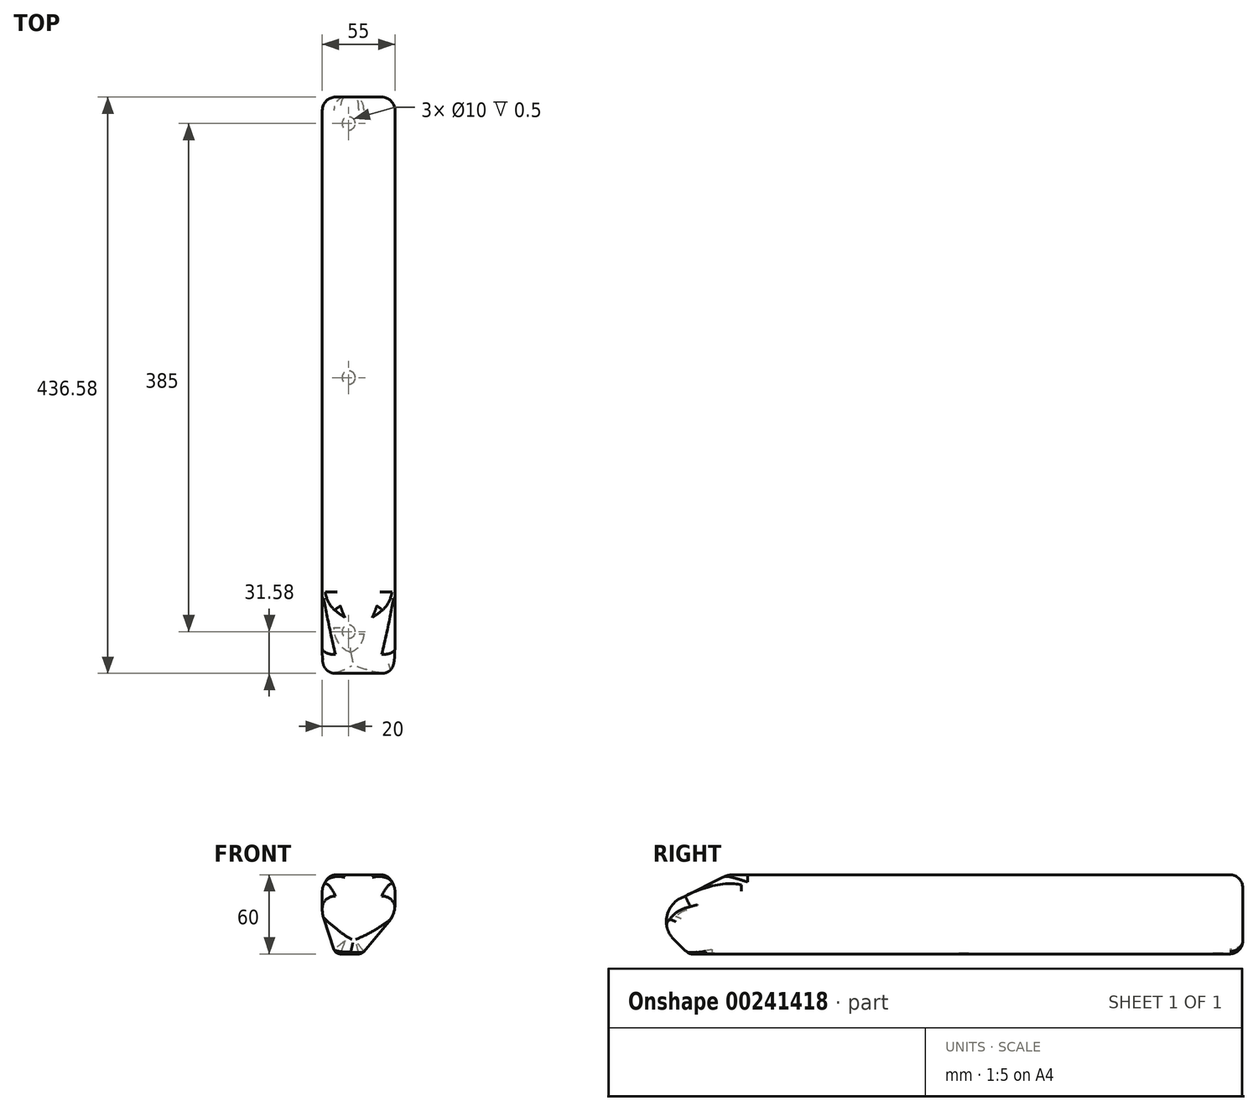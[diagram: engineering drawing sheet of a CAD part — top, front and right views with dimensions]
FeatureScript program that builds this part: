
annotation { "Feature Type Name" : "Feature", "Feature Type Description" : "" }
export const myFeature = defineFeature(function(context is Context, id is Id, definition is map)
    precondition{}
    {
        {
            var Q0;
            Q0=qCreatedBy(makeId("Top.planeOp"),FACE);
            var sketch = newSketch(context, id + "F0", { "sketchPlane" : qUnion([Q0])});
            skLineSegment(sketch, "E0.bottom", {"start": v(-27.5, 212.5) * mm, "end": v(27.5, 212.5) * mm});
            skLineSegment(sketch, "E0.top", {"start": v(-27.5, -237.5) * mm, "end": v(27.5, -237.5) * mm});
            skLineSegment(sketch, "E0.left", {"start": v(-27.5, 212.5) * mm, "end": v(-27.5, -237.5) * mm});
            skLineSegment(sketch, "E0.right", {"start": v(27.5, 212.5) * mm, "end": v(27.5, -237.5) * mm});
            skPoint(sketch, "E0.middle", {"position": v(0, -12.5) * mm});
            skSolve(sketch);
        }
        {
            var Q0;
            Q0 = qSketchRegion(id + "F0", true);
            extrude(context, id + "F1", {"entities" : qUnion([Q0]), "depth" : 60 * mm});
        }
        {
            var Q0;
            Q0=makeQuery(id+"F1.opExtrude","CAP_FACE",FACE,{"disambiguationData":[OSD([sQuery(id+"F0.wireOp",EDGE,"E0.bottom"),sQuery(id+"F0.wireOp",EDGE,"E0.top"),sQuery(id+"F0.wireOp",EDGE,"E0.left"),sQuery(id+"F0.wireOp",EDGE,"E0.right")])],"isStart":true});
            var sketch = newSketch(context, id + "F2", { "sketchPlane" : qUnion([Q0])});
            skCircle(sketch, "E1", {"center": v(-7.5, 192.5) * mm, "radius": 5 * mm});
            skCircle(sketch, "E2", {"center": v(-7.5, -192.5) * mm, "radius": 5 * mm});
            skCircle(sketch, "E3", {"center": v(-7.5, 0) * mm, "radius": 5 * mm});
            skSolve(sketch);
        }
        {
            var Q0;
            Q0 = qSketchRegion(id + "F2", true);
            extrude(context, id + "F3", {"entities" : qUnion([Q0]), "operationType" : NewBodyOperationType.REMOVE, "oppositeDirection" : true, "depth" : .5 * mm});
        }
        {
            var Q0;
            Q0=makeQuery(id+"F1.opExtrude","CAP_EDGE",EDGE,{"disambiguationData":[OSD([sQuery(id+"F0.wireOp",EDGE,"E0.top")])],"isStart":false});
            chamfer(context, id + "F4", {"entities" : qUnion([Q0]), "chamferType" : ChamferType.TWO_OFFSETS, "width1" : 60 * mm, "oppositeDirection" : false, "width2" : 30 * mm});
        }
        {
            var Q0;
            Q0=makeQuery(id+"F1.opExtrude","CAP_EDGE",EDGE,{"disambiguationData":[OSD([sQuery(id+"F0.wireOp",EDGE,"E0.top")])],"isStart":true});
            chamfer(context, id + "F5", {"entities" : qUnion([Q0]), "chamferType" : ChamferType.TWO_OFFSETS, "width1" : 30 * mm, "oppositeDirection" : false, "width2" : 30 * mm, "tangentPropagation" : true});
        }
        {
            var Q0;
            Q0=makeQuery(id+"F1.opExtrude","CAP_EDGE",EDGE,{"disambiguationData":[OSD([sQuery(id+"F0.wireOp",EDGE,"E0.left")])],"isStart":true});
            chamfer(context, id + "F6", {"entities" : qUnion([Q0]), "chamferType" : ChamferType.TWO_OFFSETS, "width1" : 30 * mm, "oppositeDirection" : false, "width2" : 10 * mm, "tangentPropagation" : true});
        }
        {
            var Q0;
            Q0=makeQuery(id+"F1.opExtrude","CAP_EDGE",EDGE,{"disambiguationData":[OSD([sQuery(id+"F0.wireOp",EDGE,"E0.right")])],"isStart":true});
            chamfer(context, id + "F7", {"entities" : qUnion([Q0]), "chamferType" : ChamferType.TWO_OFFSETS, "width1" : 25 * mm, "oppositeDirection" : false, "width2" : 30 * mm, "tangentPropagation" : true});
        }
        {
            var Q0;
            Q0=makeQuery(id+"F1.opExtrude","CAP_EDGE",EDGE,{"disambiguationData":[OSD([sQuery(id+"F0.wireOp",EDGE,"E0.left")])],"isStart":false});
            var Q1;
            Q1=makeQuery(id+"F1.opExtrude","CAP_EDGE",EDGE,{"disambiguationData":[OSD([sQuery(id+"F0.wireOp",EDGE,"E0.right")])],"isStart":false});
            chamfer(context, id + "F8", {"entities" : qUnion([Q0, Q1]), "chamferType" : ChamferType.TWO_OFFSETS, "width1" : 5 * mm, "oppositeDirection" : false, "width2" : 10 * mm, "tangentPropagation" : true});
        }
        {
            var Q0;
            {var subQ0=sQuery(id+"F0.wireOp",EDGE,"E0.top");Q0=makeQuery(id+"F4.opChamfer","BLEND_EDGE",EDGE,{"blendedFrom":[makeQuery(id+"F1.opExtrude","CAP_EDGE",EDGE,{"disambiguationData":[OSD([subQ0])],"isStart":false}),makeQuery(id+"F1.opExtrude","CAP_FACE",FACE,{"disambiguationData":[OSD([sQuery(id+"F0.wireOp",EDGE,"E0.bottom"),subQ0,sQuery(id+"F0.wireOp",EDGE,"E0.left"),sQuery(id+"F0.wireOp",EDGE,"E0.right")])],"isStart":false})],"blendedInto":[makeQuery(id+"F1.opExtrude","CAP_FACE",FACE,{"disambiguationData":[OSD([sQuery(id+"F0.wireOp",EDGE,"E0.bottom"),subQ0,sQuery(id+"F0.wireOp",EDGE,"E0.left"),sQuery(id+"F0.wireOp",EDGE,"E0.right")])],"isStart":false})]});}
            var Q1;
            {var subQ0=sQuery(id+"F0.wireOp",EDGE,"E0.top");Q1=makeQuery(id+"F5.opChamfer","BLEND_EDGE",EDGE,{"blendedFrom":[makeQuery(id+"F1.opExtrude","CAP_EDGE",EDGE,{"disambiguationData":[OSD([subQ0])],"isStart":true}),makeQuery(id+"F4.opChamfer","BLEND_FACE",FACE,{"disambiguationData":[OSD([subQ0])]})],"blendedInto":[makeQuery(id+"F4.opChamfer","BLEND_FACE",FACE,{"disambiguationData":[OSD([subQ0])]})]});}
            var Q2;
            {var subQ0=sQuery(id+"F0.wireOp",EDGE,"E0.top");Q2=makeQuery(id+"F5.opChamfer","BLEND_EDGE",EDGE,{"blendedFrom":[makeQuery(id+"F1.opExtrude","CAP_EDGE",EDGE,{"disambiguationData":[OSD([subQ0])],"isStart":true}),makeQuery(id+"F1.opExtrude","CAP_FACE",FACE,{"disambiguationData":[OSD([sQuery(id+"F0.wireOp",EDGE,"E0.bottom"),subQ0,sQuery(id+"F0.wireOp",EDGE,"E0.left"),sQuery(id+"F0.wireOp",EDGE,"E0.right")])],"isStart":true})],"blendedInto":[makeQuery(id+"F1.opExtrude","CAP_FACE",FACE,{"disambiguationData":[OSD([sQuery(id+"F0.wireOp",EDGE,"E0.bottom"),subQ0,sQuery(id+"F0.wireOp",EDGE,"E0.left"),sQuery(id+"F0.wireOp",EDGE,"E0.right")])],"isStart":true})]});}
            var Q3;
            Q3=makeQuery(id+"F7.opChamfer","BLEND_EDGE",EDGE,{"blendedFrom":[makeQuery(id+"F1.opExtrude","CAP_EDGE",EDGE,{"disambiguationData":[OSD([sQuery(id+"F0.wireOp",EDGE,"E0.right")])],"isStart":true}),makeQuery(id+"F5.opChamfer","BLEND_FACE",FACE,{"disambiguationData":[OSD([sQuery(id+"F0.wireOp",EDGE,"E0.top")])]})],"blendedInto":[makeQuery(id+"F5.opChamfer","BLEND_FACE",FACE,{"disambiguationData":[OSD([sQuery(id+"F0.wireOp",EDGE,"E0.top")])]})]});
            var Q4;
            Q4=makeQuery(id+"F6.opChamfer","BLEND_EDGE",EDGE,{"blendedFrom":[makeQuery(id+"F1.opExtrude","CAP_EDGE",EDGE,{"disambiguationData":[OSD([sQuery(id+"F0.wireOp",EDGE,"E0.left")])],"isStart":true}),makeQuery(id+"F5.opChamfer","BLEND_FACE",FACE,{"disambiguationData":[OSD([sQuery(id+"F0.wireOp",EDGE,"E0.top")])]})],"blendedInto":[makeQuery(id+"F5.opChamfer","BLEND_FACE",FACE,{"disambiguationData":[OSD([sQuery(id+"F0.wireOp",EDGE,"E0.top")])]})]});
            var Q5;
            Q5=makeQuery(id+"F8.opChamfer","BLEND_EDGE",EDGE,{"blendedFrom":[makeQuery(id+"F1.opExtrude","CAP_EDGE",EDGE,{"disambiguationData":[OSD([sQuery(id+"F0.wireOp",EDGE,"E0.left")])],"isStart":false}),makeQuery(id+"F4.opChamfer","BLEND_FACE",FACE,{"disambiguationData":[OSD([sQuery(id+"F0.wireOp",EDGE,"E0.top")])]})],"blendedInto":[makeQuery(id+"F4.opChamfer","BLEND_FACE",FACE,{"disambiguationData":[OSD([sQuery(id+"F0.wireOp",EDGE,"E0.top")])]})]});
            var Q6;
            Q6=makeQuery(id+"F8.opChamfer","BLEND_EDGE",EDGE,{"blendedFrom":[makeQuery(id+"F1.opExtrude","CAP_EDGE",EDGE,{"disambiguationData":[OSD([sQuery(id+"F0.wireOp",EDGE,"E0.right")])],"isStart":false}),makeQuery(id+"F4.opChamfer","BLEND_FACE",FACE,{"disambiguationData":[OSD([sQuery(id+"F0.wireOp",EDGE,"E0.top")])]})],"blendedInto":[makeQuery(id+"F4.opChamfer","BLEND_FACE",FACE,{"disambiguationData":[OSD([sQuery(id+"F0.wireOp",EDGE,"E0.top")])]})]});
            fillet(context, id + "F9", {"entities" : qUnion([Q0, Q1, Q2, Q3, Q4, Q5, Q6]), "radius" : 19.5 * mm, "tangentPropagation" : true, "allowEdgeOverflow" : false});
        }
        {
            var Q0;
            {var subQ0=sQuery(id+"F0.wireOp",EDGE,"E0.left");Q0=makeQuery(id+"F6.opChamfer","BLEND_EDGE",EDGE,{"blendedFrom":[makeQuery(id+"F1.opExtrude","CAP_EDGE",EDGE,{"disambiguationData":[OSD([subQ0])],"isStart":true}),makeQuery(id+"F1.opExtrude","CAP_FACE",FACE,{"disambiguationData":[OSD([sQuery(id+"F0.wireOp",EDGE,"E0.bottom"),sQuery(id+"F0.wireOp",EDGE,"E0.top"),subQ0,sQuery(id+"F0.wireOp",EDGE,"E0.right")])],"isStart":true})],"blendedInto":[makeQuery(id+"F1.opExtrude","CAP_FACE",FACE,{"disambiguationData":[OSD([sQuery(id+"F0.wireOp",EDGE,"E0.bottom"),sQuery(id+"F0.wireOp",EDGE,"E0.top"),subQ0,sQuery(id+"F0.wireOp",EDGE,"E0.right")])],"isStart":true})]});}
            var Q1;
            {var subQ0=sQuery(id+"F0.wireOp",EDGE,"E0.right");Q1=makeQuery(id+"F7.opChamfer","BLEND_EDGE",EDGE,{"blendedFrom":[makeQuery(id+"F1.opExtrude","CAP_EDGE",EDGE,{"disambiguationData":[OSD([subQ0])],"isStart":true}),makeQuery(id+"F1.opExtrude","CAP_FACE",FACE,{"disambiguationData":[OSD([sQuery(id+"F0.wireOp",EDGE,"E0.bottom"),sQuery(id+"F0.wireOp",EDGE,"E0.top"),sQuery(id+"F0.wireOp",EDGE,"E0.left"),subQ0])],"isStart":true})],"blendedInto":[makeQuery(id+"F1.opExtrude","CAP_FACE",FACE,{"disambiguationData":[OSD([sQuery(id+"F0.wireOp",EDGE,"E0.bottom"),sQuery(id+"F0.wireOp",EDGE,"E0.top"),sQuery(id+"F0.wireOp",EDGE,"E0.left"),subQ0])],"isStart":true})]});}
            fillet(context, id + "F10", {"entities" : qUnion([Q0, Q1]), "radius" : 5 * mm, "tangentPropagation" : true, "allowEdgeOverflow" : false});
        }
        {
            var Q0;
            {var subQ0=sQuery(id+"F0.wireOp",EDGE,"E0.left");Q0=makeQuery(id+"F9.opFillet","BLEND_EDGE",EDGE,{"blendedFrom":[makeQuery(id+"F6.opChamfer","BLEND_EDGE",EDGE,{"blendedFrom":[makeQuery(id+"F1.opExtrude","CAP_EDGE",EDGE,{"disambiguationData":[OSD([subQ0])],"isStart":true}),makeQuery(id+"F5.opChamfer","BLEND_FACE",FACE,{"disambiguationData":[OSD([sQuery(id+"F0.wireOp",EDGE,"E0.top")])]})],"blendedInto":[makeQuery(id+"F5.opChamfer","BLEND_FACE",FACE,{"disambiguationData":[OSD([sQuery(id+"F0.wireOp",EDGE,"E0.top")])]})]}),makeQuery(id+"F6.opChamfer","BLEND_FACE",FACE,{"disambiguationData":[OSD([subQ0])]})],"blendedInto":[makeQuery(id+"F6.opChamfer","BLEND_FACE",FACE,{"disambiguationData":[OSD([subQ0])]})]});}
            var Q1;
            {var subQ0=sQuery(id+"F0.wireOp",EDGE,"E0.top");Q1=makeQuery(id+"F9.opFillet","BLEND_EDGE",EDGE,{"blendedFrom":[makeQuery(id+"F5.opChamfer","BLEND_EDGE",EDGE,{"blendedFrom":[makeQuery(id+"F1.opExtrude","CAP_EDGE",EDGE,{"disambiguationData":[OSD([subQ0])],"isStart":true}),makeQuery(id+"F4.opChamfer","BLEND_FACE",FACE,{"disambiguationData":[OSD([subQ0])]})],"blendedInto":[makeQuery(id+"F4.opChamfer","BLEND_FACE",FACE,{"disambiguationData":[OSD([subQ0])]})]}),makeQuery(id+"F1.opExtrude","SWEPT_FACE",FACE,{"disambiguationData":[OSD([sQuery(id+"F0.wireOp",EDGE,"E0.left")])]})],"blendedInto":[makeQuery(id+"F1.opExtrude","SWEPT_FACE",FACE,{"disambiguationData":[OSD([sQuery(id+"F0.wireOp",EDGE,"E0.left")])]})]});}
            var Q2;
            {var subQ0=sQuery(id+"F0.wireOp",EDGE,"E0.left");Q2=makeQuery(id+"F9.opFillet","BLEND_EDGE",EDGE,{"blendedFrom":[makeQuery(id+"F8.opChamfer","BLEND_EDGE",EDGE,{"blendedFrom":[makeQuery(id+"F1.opExtrude","CAP_EDGE",EDGE,{"disambiguationData":[OSD([subQ0])],"isStart":false}),makeQuery(id+"F4.opChamfer","BLEND_FACE",FACE,{"disambiguationData":[OSD([sQuery(id+"F0.wireOp",EDGE,"E0.top")])]})],"blendedInto":[makeQuery(id+"F4.opChamfer","BLEND_FACE",FACE,{"disambiguationData":[OSD([sQuery(id+"F0.wireOp",EDGE,"E0.top")])]})]}),makeQuery(id+"F1.opExtrude","SWEPT_FACE",FACE,{"disambiguationData":[OSD([subQ0])]})],"blendedInto":[makeQuery(id+"F1.opExtrude","SWEPT_FACE",FACE,{"disambiguationData":[OSD([subQ0])]})]});}
            var Q3;
            {var subQ0=sQuery(id+"F0.wireOp",EDGE,"E0.left");Q3=makeQuery(id+"F9.opFillet","BLEND_EDGE",EDGE,{"blendedFrom":[makeQuery(id+"F8.opChamfer","BLEND_EDGE",EDGE,{"blendedFrom":[makeQuery(id+"F1.opExtrude","CAP_EDGE",EDGE,{"disambiguationData":[OSD([subQ0])],"isStart":false}),makeQuery(id+"F4.opChamfer","BLEND_FACE",FACE,{"disambiguationData":[OSD([sQuery(id+"F0.wireOp",EDGE,"E0.top")])]})],"blendedInto":[makeQuery(id+"F4.opChamfer","BLEND_FACE",FACE,{"disambiguationData":[OSD([sQuery(id+"F0.wireOp",EDGE,"E0.top")])]})]}),makeQuery(id+"F8.opChamfer","BLEND_FACE",FACE,{"disambiguationData":[OSD([subQ0])]})],"blendedInto":[makeQuery(id+"F8.opChamfer","BLEND_FACE",FACE,{"disambiguationData":[OSD([subQ0])]})]});}
            var Q4;
            {var subQ0=sQuery(id+"F0.wireOp",EDGE,"E0.right");Q4=makeQuery(id+"F9.opFillet","BLEND_EDGE",EDGE,{"blendedFrom":[makeQuery(id+"F8.opChamfer","BLEND_EDGE",EDGE,{"blendedFrom":[makeQuery(id+"F1.opExtrude","CAP_EDGE",EDGE,{"disambiguationData":[OSD([subQ0])],"isStart":false}),makeQuery(id+"F4.opChamfer","BLEND_FACE",FACE,{"disambiguationData":[OSD([sQuery(id+"F0.wireOp",EDGE,"E0.top")])]})],"blendedInto":[makeQuery(id+"F4.opChamfer","BLEND_FACE",FACE,{"disambiguationData":[OSD([sQuery(id+"F0.wireOp",EDGE,"E0.top")])]})]}),makeQuery(id+"F8.opChamfer","BLEND_FACE",FACE,{"disambiguationData":[OSD([subQ0])]})],"blendedInto":[makeQuery(id+"F8.opChamfer","BLEND_FACE",FACE,{"disambiguationData":[OSD([subQ0])]})]});}
            var Q5;
            {var subQ0=sQuery(id+"F0.wireOp",EDGE,"E0.right");Q5=makeQuery(id+"F9.opFillet","BLEND_EDGE",EDGE,{"blendedFrom":[makeQuery(id+"F8.opChamfer","BLEND_EDGE",EDGE,{"blendedFrom":[makeQuery(id+"F1.opExtrude","CAP_EDGE",EDGE,{"disambiguationData":[OSD([subQ0])],"isStart":false}),makeQuery(id+"F4.opChamfer","BLEND_FACE",FACE,{"disambiguationData":[OSD([sQuery(id+"F0.wireOp",EDGE,"E0.top")])]})],"blendedInto":[makeQuery(id+"F4.opChamfer","BLEND_FACE",FACE,{"disambiguationData":[OSD([sQuery(id+"F0.wireOp",EDGE,"E0.top")])]})]}),makeQuery(id+"F1.opExtrude","SWEPT_FACE",FACE,{"disambiguationData":[OSD([subQ0])]})],"blendedInto":[makeQuery(id+"F1.opExtrude","SWEPT_FACE",FACE,{"disambiguationData":[OSD([subQ0])]})]});}
            var Q6;
            {var subQ0=sQuery(id+"F0.wireOp",EDGE,"E0.top");Q6=makeQuery(id+"F9.opFillet","BLEND_EDGE",EDGE,{"blendedFrom":[makeQuery(id+"F5.opChamfer","BLEND_EDGE",EDGE,{"blendedFrom":[makeQuery(id+"F1.opExtrude","CAP_EDGE",EDGE,{"disambiguationData":[OSD([subQ0])],"isStart":true}),makeQuery(id+"F4.opChamfer","BLEND_FACE",FACE,{"disambiguationData":[OSD([subQ0])]})],"blendedInto":[makeQuery(id+"F4.opChamfer","BLEND_FACE",FACE,{"disambiguationData":[OSD([subQ0])]})]}),makeQuery(id+"F1.opExtrude","SWEPT_FACE",FACE,{"disambiguationData":[OSD([sQuery(id+"F0.wireOp",EDGE,"E0.right")])]})],"blendedInto":[makeQuery(id+"F1.opExtrude","SWEPT_FACE",FACE,{"disambiguationData":[OSD([sQuery(id+"F0.wireOp",EDGE,"E0.right")])]})]});}
            var Q7;
            {var subQ0=sQuery(id+"F0.wireOp",EDGE,"E0.right");Q7=makeQuery(id+"F9.opFillet","BLEND_EDGE",EDGE,{"blendedFrom":[makeQuery(id+"F7.opChamfer","BLEND_EDGE",EDGE,{"blendedFrom":[makeQuery(id+"F1.opExtrude","CAP_EDGE",EDGE,{"disambiguationData":[OSD([subQ0])],"isStart":true}),makeQuery(id+"F5.opChamfer","BLEND_FACE",FACE,{"disambiguationData":[OSD([sQuery(id+"F0.wireOp",EDGE,"E0.top")])]})],"blendedInto":[makeQuery(id+"F5.opChamfer","BLEND_FACE",FACE,{"disambiguationData":[OSD([sQuery(id+"F0.wireOp",EDGE,"E0.top")])]})]}),makeQuery(id+"F7.opChamfer","BLEND_FACE",FACE,{"disambiguationData":[OSD([subQ0])]})],"blendedInto":[makeQuery(id+"F7.opChamfer","BLEND_FACE",FACE,{"disambiguationData":[OSD([subQ0])]})]});}
            fillet(context, id + "F11", {"entities" : qUnion([Q0, Q1, Q2, Q3, Q4, Q5, Q6, Q7]), "radius" : 10 * mm, "tangentPropagation" : true, "allowEdgeOverflow" : false});
        }
        {
            var Q0;
            {var subQ0=sQuery(id+"F0.wireOp",EDGE,"E0.right");Q0=makeQuery(id+"F7.opChamfer","BLEND_EDGE",EDGE,{"blendedFrom":[makeQuery(id+"F1.opExtrude","CAP_EDGE",EDGE,{"disambiguationData":[OSD([subQ0])],"isStart":true}),makeQuery(id+"F1.opExtrude","SWEPT_FACE",FACE,{"disambiguationData":[OSD([subQ0])]})],"blendedInto":[makeQuery(id+"F1.opExtrude","SWEPT_FACE",FACE,{"disambiguationData":[OSD([subQ0])]})]});}
            var Q1;
            {var subQ0=sQuery(id+"F0.wireOp",EDGE,"E0.right");var subQ1=makeQuery(id+"F1.opExtrude","SWEPT_FACE",FACE,{"disambiguationData":[OSD([subQ0])]});Q1=makeQuery(id+"F11.opFillet","BLEND_EDGE",EDGE,{"blendedFrom":[makeQuery(id+"F8.opChamfer","BLEND_EDGE",EDGE,{"blendedFrom":[makeQuery(id+"F1.opExtrude","CAP_EDGE",EDGE,{"disambiguationData":[OSD([subQ0])],"isStart":false}),subQ1],"blendedInto":[subQ1]}),subQ1],"blendedInto":[subQ1]});}
            var Q2;
            {var subQ0=sQuery(id+"F0.wireOp",EDGE,"E0.right");Q2=makeQuery(id+"F11.opFillet","BLEND_EDGE",EDGE,{"blendedFrom":[makeQuery(id+"F8.opChamfer","BLEND_EDGE",EDGE,{"blendedFrom":[makeQuery(id+"F1.opExtrude","CAP_EDGE",EDGE,{"disambiguationData":[OSD([subQ0])],"isStart":false}),makeQuery(id+"F1.opExtrude","SWEPT_FACE",FACE,{"disambiguationData":[OSD([subQ0])]})],"blendedInto":[makeQuery(id+"F1.opExtrude","SWEPT_FACE",FACE,{"disambiguationData":[OSD([subQ0])]})]}),makeQuery(id+"F8.opChamfer","BLEND_FACE",FACE,{"disambiguationData":[OSD([subQ0])]})],"blendedInto":[makeQuery(id+"F8.opChamfer","BLEND_FACE",FACE,{"disambiguationData":[OSD([subQ0])]})]});}
            var Q3;
            {var subQ0=sQuery(id+"F0.wireOp",EDGE,"E0.right");Q3=makeQuery(id+"F10.opFillet","BLEND_EDGE",EDGE,{"blendedFrom":[makeQuery(id+"F7.opChamfer","BLEND_EDGE",EDGE,{"blendedFrom":[makeQuery(id+"F1.opExtrude","CAP_EDGE",EDGE,{"disambiguationData":[OSD([subQ0])],"isStart":true}),makeQuery(id+"F1.opExtrude","CAP_FACE",FACE,{"disambiguationData":[OSD([sQuery(id+"F0.wireOp",EDGE,"E0.bottom"),sQuery(id+"F0.wireOp",EDGE,"E0.top"),sQuery(id+"F0.wireOp",EDGE,"E0.left"),subQ0])],"isStart":true})],"blendedInto":[makeQuery(id+"F1.opExtrude","CAP_FACE",FACE,{"disambiguationData":[OSD([sQuery(id+"F0.wireOp",EDGE,"E0.bottom"),sQuery(id+"F0.wireOp",EDGE,"E0.top"),sQuery(id+"F0.wireOp",EDGE,"E0.left"),subQ0])],"isStart":true})]}),makeQuery(id+"F7.opChamfer","BLEND_FACE",FACE,{"disambiguationData":[OSD([subQ0])]})],"blendedInto":[makeQuery(id+"F7.opChamfer","BLEND_FACE",FACE,{"disambiguationData":[OSD([subQ0])]})]});}
            var Q4;
            {var subQ0=sQuery(id+"F0.wireOp",EDGE,"E0.left");Q4=makeQuery(id+"F10.opFillet","BLEND_EDGE",EDGE,{"blendedFrom":[makeQuery(id+"F6.opChamfer","BLEND_EDGE",EDGE,{"blendedFrom":[makeQuery(id+"F1.opExtrude","CAP_EDGE",EDGE,{"disambiguationData":[OSD([subQ0])],"isStart":true}),makeQuery(id+"F1.opExtrude","CAP_FACE",FACE,{"disambiguationData":[OSD([sQuery(id+"F0.wireOp",EDGE,"E0.bottom"),sQuery(id+"F0.wireOp",EDGE,"E0.top"),subQ0,sQuery(id+"F0.wireOp",EDGE,"E0.right")])],"isStart":true})],"blendedInto":[makeQuery(id+"F1.opExtrude","CAP_FACE",FACE,{"disambiguationData":[OSD([sQuery(id+"F0.wireOp",EDGE,"E0.bottom"),sQuery(id+"F0.wireOp",EDGE,"E0.top"),subQ0,sQuery(id+"F0.wireOp",EDGE,"E0.right")])],"isStart":true})]}),makeQuery(id+"F6.opChamfer","BLEND_FACE",FACE,{"disambiguationData":[OSD([subQ0])]})],"blendedInto":[makeQuery(id+"F6.opChamfer","BLEND_FACE",FACE,{"disambiguationData":[OSD([subQ0])]})]});}
            var Q5;
            {var subQ0=sQuery(id+"F0.wireOp",EDGE,"E0.left");Q5=makeQuery(id+"F6.opChamfer","BLEND_EDGE",EDGE,{"blendedFrom":[makeQuery(id+"F1.opExtrude","CAP_EDGE",EDGE,{"disambiguationData":[OSD([subQ0])],"isStart":true}),makeQuery(id+"F1.opExtrude","SWEPT_FACE",FACE,{"disambiguationData":[OSD([subQ0])]})],"blendedInto":[makeQuery(id+"F1.opExtrude","SWEPT_FACE",FACE,{"disambiguationData":[OSD([subQ0])]})]});}
            var Q6;
            {var subQ0=sQuery(id+"F0.wireOp",EDGE,"E0.left");var subQ1=makeQuery(id+"F1.opExtrude","SWEPT_FACE",FACE,{"disambiguationData":[OSD([subQ0])]});Q6=makeQuery(id+"F11.opFillet","BLEND_EDGE",EDGE,{"blendedFrom":[makeQuery(id+"F8.opChamfer","BLEND_EDGE",EDGE,{"blendedFrom":[makeQuery(id+"F1.opExtrude","CAP_EDGE",EDGE,{"disambiguationData":[OSD([subQ0])],"isStart":false}),subQ1],"blendedInto":[subQ1]}),subQ1],"blendedInto":[subQ1]});}
            fillet(context, id + "F12", {"entities" : qUnion([Q0, Q1, Q2, Q3, Q4, Q5, Q6]), "radius" : 20 * mm, "allowEdgeOverflow" : false});
        }
        {
            var Q0;
            {var subQ0=sQuery(id+"F0.wireOp",EDGE,"E0.right");Q0=makeQuery(id+"F8.opChamfer","BLEND_EDGE",EDGE,{"blendedFrom":[makeQuery(id+"F1.opExtrude","CAP_EDGE",EDGE,{"disambiguationData":[OSD([subQ0])],"isStart":false}),makeQuery(id+"F1.opExtrude","CAP_FACE",FACE,{"disambiguationData":[OSD([sQuery(id+"F0.wireOp",EDGE,"E0.bottom"),sQuery(id+"F0.wireOp",EDGE,"E0.top"),sQuery(id+"F0.wireOp",EDGE,"E0.left"),subQ0])],"isStart":false})],"blendedInto":[makeQuery(id+"F1.opExtrude","CAP_FACE",FACE,{"disambiguationData":[OSD([sQuery(id+"F0.wireOp",EDGE,"E0.bottom"),sQuery(id+"F0.wireOp",EDGE,"E0.top"),sQuery(id+"F0.wireOp",EDGE,"E0.left"),subQ0])],"isStart":false})]});}
            var Q1;
            {var subQ0=sQuery(id+"F0.wireOp",EDGE,"E0.left");Q1=makeQuery(id+"F8.opChamfer","BLEND_EDGE",EDGE,{"blendedFrom":[makeQuery(id+"F1.opExtrude","CAP_EDGE",EDGE,{"disambiguationData":[OSD([subQ0])],"isStart":false}),makeQuery(id+"F1.opExtrude","CAP_FACE",FACE,{"disambiguationData":[OSD([sQuery(id+"F0.wireOp",EDGE,"E0.bottom"),sQuery(id+"F0.wireOp",EDGE,"E0.top"),subQ0,sQuery(id+"F0.wireOp",EDGE,"E0.right")])],"isStart":false})],"blendedInto":[makeQuery(id+"F1.opExtrude","CAP_FACE",FACE,{"disambiguationData":[OSD([sQuery(id+"F0.wireOp",EDGE,"E0.bottom"),sQuery(id+"F0.wireOp",EDGE,"E0.top"),subQ0,sQuery(id+"F0.wireOp",EDGE,"E0.right")])],"isStart":false})]});}
            fillet(context, id + "F13", {"entities" : qUnion([Q0, Q1]), "radius" : 10 * mm, "tangentPropagation" : true, "allowEdgeOverflow" : false});
        }
        {
            var Q0;
            Q0=makeQuery(id+"F1.opExtrude","SWEPT_FACE",FACE,{"disambiguationData":[OSD([sQuery(id+"F0.wireOp",EDGE,"E0.bottom")])]});
            fillet(context, id + "F14", {"entities" : qUnion([Q0]), "radius" : 10 * mm, "tangentPropagation" : true, "allowEdgeOverflow" : false});
        }
    });
